# Revit family: РИДАН_ Клапан редукционный Ридан 7biz
name_source: partatom
category: Арматура трубопроводов
units: mm (PartAtom-declared; Revit-internal decimal feet)

## family parameters
Всегда вертикально = Да
На основе рабочей плоскости = Нет
Общий = Нет
При загрузке вырезать с полостями = Нет
Размер круглого соединителя = Использовать диаметр
Тип детали = Вставляется

## types (6) — shared parameters
ADSK_Версия Revit = 2019
ADSK_Версия семейства = 1.0
ADSK_Единица измерения = шт.
ADSK_Завод-изготовитель = ООО «Ридан-Трейд»
ADSK_Количество = 1
ADSK_Потеря давления жидкости = 0.0 Па
ADSK_Расход жидкости = 0 м³/ч
LT = Table
URL = https://ridan.ru
h = 75 мм
q = 18 мм
r = 17 мм
Изготовитель = ООО «Ридан-Трейд»

## per-type parameters (varying)
- DN 15: ADSK_Диаметр условный=15 мм; ADSK_Код изделия=082X4140R; ADSK_Марка=7biz DN15; ADSK_Масса=0.37; ADSK_Наименование=Клапан редукционный 7biz PN16 DN15; ADSK_Пропускная способность=1.8 м³/ч; a=11 мм; b=2 мм; c=45 мм; d=22 мм; e=73 мм; f=12 мм; g=13 мм; i=27 мм; j=9 мм; k=15.00°; l=21 мм; m=15 мм; n=10 мм; o=28 мм; p=5 мм; p1=33 мм; s=69.00°; t=25 мм; u=35 мм; v=21 мм
- DN 20: ADSK_Диаметр условный=20 мм; ADSK_Код изделия=082X4141R; ADSK_Марка=7biz DN20; ADSK_Масса=0.415; ADSK_Наименование=Клапан редукционный 7biz PN16 DN20; ADSK_Пропускная способность=2.2 м³/ч; a=16 мм; b=2 мм; c=40 мм; d=20 мм; e=75 мм; f=15 мм; g=16 мм; i=32 мм; j=12 мм; k=15.00°; l=26 мм; m=20 мм; n=8 мм; o=31 мм; p=5 мм; p1=36 мм; s=65.00°; t=25 мм; u=38 мм; v=26 мм
- DN 25: ADSK_Диаметр условный=25 мм; ADSK_Код изделия=082X4142R; ADSK_Марка=7biz DN25; ADSK_Масса=0.45; ADSK_Наименование=Клапан редукционный 7biz PN16 DN25; ADSK_Пропускная способность=2.4 м³/ч; a=16 мм; b=3 мм; c=43 мм; d=22 мм; e=75 мм; f=16 мм; g=19 мм; i=37 мм; j=13 мм; k=15.00°; l=34 мм; m=25 мм; n=8 мм; o=34 мм; p=5 мм; p1=38 мм; s=65.00°; t=27 мм; u=41 мм; v=34 мм
- DN 32: ADSK_Диаметр условный=32 мм; ADSK_Код изделия=082X4143R; ADSK_Марка=7biz DN32; ADSK_Масса=1.05; ADSK_Наименование=Клапан редукционный 7biz PN16 DN32; ADSK_Пропускная способность=4.5 м³/ч; a=14 мм; b=5 мм; c=65 мм; d=33 мм; e=73 мм; f=22 мм; g=24 мм; i=48 мм; j=14 мм; k=10.00°; l=34 мм; m=32 мм; n=14 мм; o=41 мм; p=4 мм; p1=45 мм; s=65.00°; t=14 мм; u=24 мм; v=10 мм
- DN 40: ADSK_Диаметр условный=40 мм; ADSK_Код изделия=082X4144R; ADSK_Марка=7biz DN40; ADSK_Масса=1.12; ADSK_Наименование=Клапан редукционный 7biz PN16 DN40; ADSK_Пропускная способность=6.3 м³/ч; a=14 мм; b=8 мм; c=63 мм; d=32 мм; e=73 мм; f=22 мм; g=27 мм; i=54 мм; j=16 мм; k=10.00°; l=48 мм; m=40 мм; n=15 мм; o=43 мм; p=4 мм; p1=47 мм; s=65.00°; t=15 мм; u=24 мм; v=10 мм
- DN 50: ADSK_Диаметр условный=50 мм; ADSK_Код изделия=082X4145R; ADSK_Марка=7biz DN50; ADSK_Масса=1.45; ADSK_Наименование=Клапан редукционный 7biz PN16 DN50; ADSK_Пропускная способность=7.5 м³/ч; a=16 мм; b=8 мм; c=65 мм; d=33 мм; e=73 мм; f=22 мм; g=33 мм; i=65 мм; j=16 мм; k=10.00°; l=60 мм; m=50 мм; n=15 мм; o=48 мм; p=4 мм; p1=52 мм; s=65.00°; t=15 мм; u=24 мм; v=10 мм
